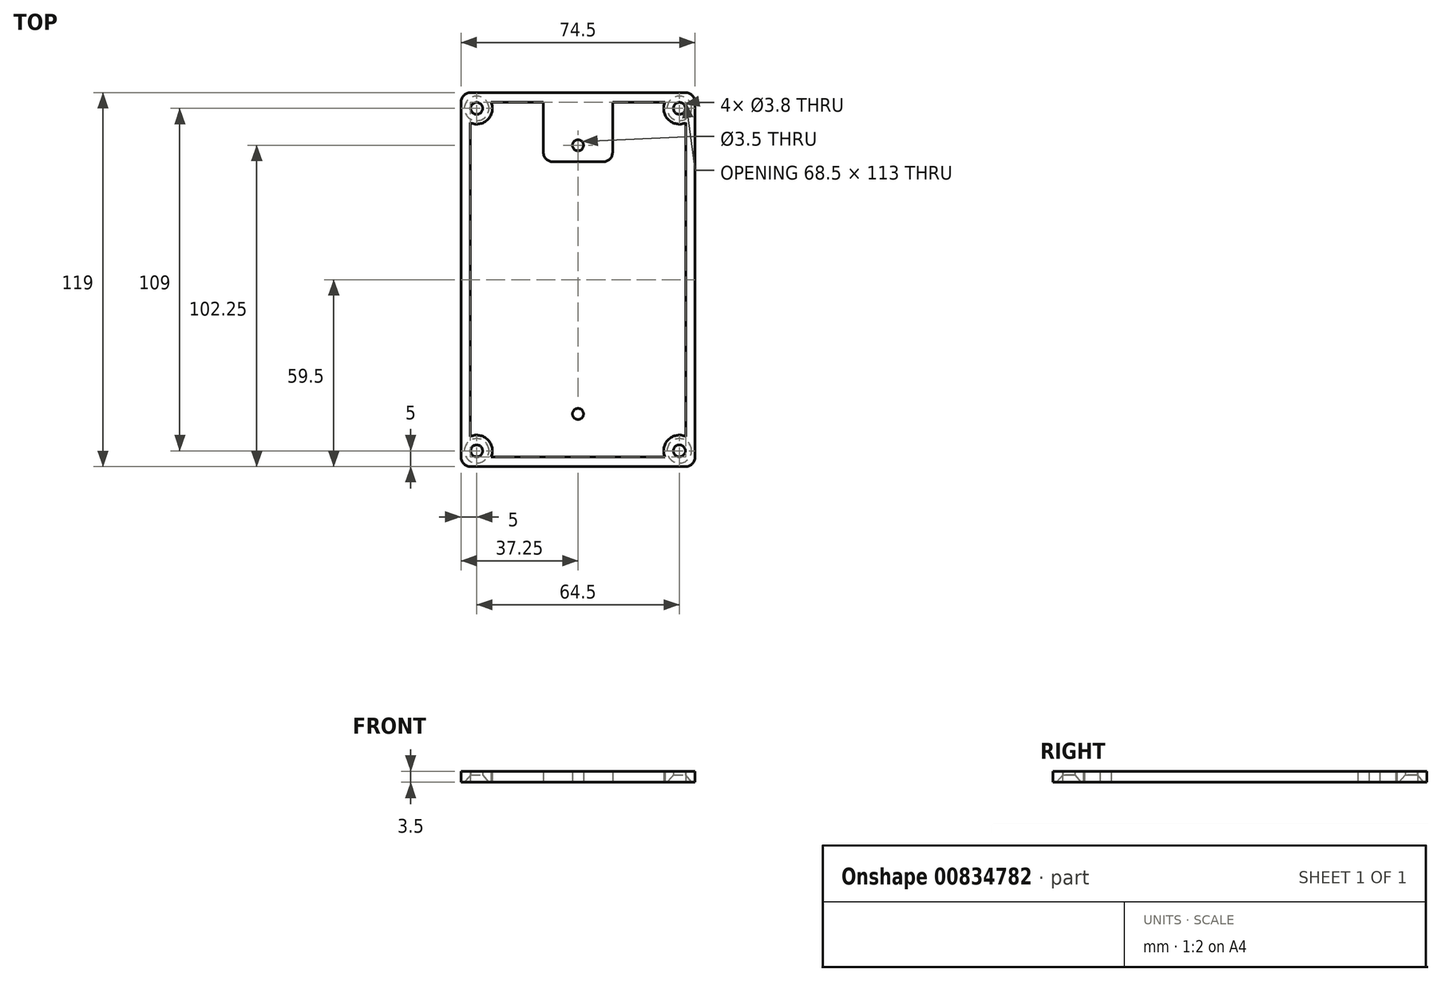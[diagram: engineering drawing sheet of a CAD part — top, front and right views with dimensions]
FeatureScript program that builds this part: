
annotation { "Feature Type Name" : "Feature", "Feature Type Description" : "" }
export const myFeature = defineFeature(function(context is Context, id is Id, definition is map)
    precondition{}
    {
        {
            var Q0;
            Q0=qCreatedBy(makeId("Top.planeOp"),FACE);
            var sketch = newSketch(context, id + "F0", { "sketchPlane" : qUnion([Q0])});
            skLineSegment(sketch, "E0.bottom", {"start": v(-37.25, 59.5) * mm, "end": v(37.25, 59.5) * mm});
            skLineSegment(sketch, "E0.top", {"start": v(-37.25, -59.5) * mm, "end": v(37.25, -59.5) * mm});
            skLineSegment(sketch, "E0.left", {"start": v(-37.25, 59.5) * mm, "end": v(-37.25, -59.5) * mm});
            skLineSegment(sketch, "E0.right", {"start": v(37.25, 59.5) * mm, "end": v(37.25, -59.5) * mm});
            skPoint(sketch, "E0.middle", {"position": v(0, 0) * mm});
            skLineSegment(sketch, "E1.bottom", {"start": v(-34.25, 56.5) * mm, "end": v(34.25, 56.5) * mm});
            skLineSegment(sketch, "E1.top", {"start": v(-34.25, -56.5) * mm, "end": v(34.25, -56.5) * mm});
            skLineSegment(sketch, "E1.left", {"start": v(-34.25, 56.5) * mm, "end": v(-34.25, -56.5) * mm});
            skLineSegment(sketch, "E1.right", {"start": v(34.25, 56.5) * mm, "end": v(34.25, -56.5) * mm});
            skCircle(sketch, "E2", {"center": v(-32.25, 54.5) * mm, "radius": 5 * mm});
            skPoint(sketch, "E2.first.point", {"position": v(-32.25, 59.5) * mm});
            skPoint(sketch, "E2.second.point", {"position": v(-33.16, 49.58) * mm});
            skPoint(sketch, "E2.third.point", {"position": v(-27.94, 51.97) * mm});
            skCircle(sketch, "E3", {"center": v(-32.25, 54.5) * mm, "radius": 1.9 * mm});
            skCircle(sketch, "E4.MirrorC", {"center": v(-32.25, -54.5) * mm, "radius": 5 * mm});
            skCircle(sketch, "E5.MirrorC", {"center": v(-32.25, -54.5) * mm, "radius": 1.9 * mm});
            skCircle(sketch, "E6.MirrorC", {"center": v(32.25, -54.5) * mm, "radius": 5 * mm});
            skCircle(sketch, "E7.MirrorC", {"center": v(32.25, -54.5) * mm, "radius": 1.9 * mm});
            skCircle(sketch, "E8.MirrorC", {"center": v(32.25, 54.5) * mm, "radius": 5 * mm});
            skCircle(sketch, "E9.MirrorC", {"center": v(32.25, 54.5) * mm, "radius": 1.9 * mm});
            skCircle(sketch, "E10", {"center": v(0, 42.75) * mm, "radius": 1.75 * mm});
            skPoint(sketch, "E10.centerSnap0", {"position": v(0, 59.5) * mm});
            skCircle(sketch, "E11.MirrorC", {"center": v(0, -42.75) * mm, "radius": 1.75 * mm});
            skLineSegment(sketch, "E12", {"start": v(-11, 56.5) * mm, "end": v(-11, 37.5) * mm});
            skLineSegment(sketch, "E13", {"start": v(-11, 37.5) * mm, "end": v(11, 37.5) * mm});
            skLineSegment(sketch, "E14", {"start": v(11, 37.5) * mm, "end": v(11, 56.5) * mm});
            skPoint(sketch, "E15", {"position": v(0, 37.5) * mm});
            skLineSegment(sketch, "E16.MirrorCS", {"start": v(11, -37.5) * mm, "end": v(11, -56.5) * mm});
            skLineSegment(sketch, "E17.MirrorCS", {"start": v(-11, -56.5) * mm, "end": v(-11, -37.5) * mm});
            skLineSegment(sketch, "E18.MirrorCS", {"start": v(-11, -37.5) * mm, "end": v(11, -37.5) * mm});
            skSolve(sketch);
        }
        {
            var Q0;
            {var subQ0=sQuery(id+"F0.wireOp",EDGE,"E0.left");var subQ1=sQuery(id+"F0.wireOp",EDGE,"E0.bottom");var subQ2=makeQuery(id+"F0.imprint","INTERSECT",VERTEX,{"derivedFrom":[subQ1,subQ0]});Q0=makeQuery(id+"F0.imprint","IMPRINT",FACE,{"disambiguationData":[TD([[makeQuery(id+"F0.imprint","IMPRINT",EDGE,{"disambiguationData":[TD([[subQ2,-1.0]])],"derivedFrom":subQ1}),-1.0]])]});}
            var Q1;
            {var subQ0=sQuery(id+"F0.wireOp",EDGE,"E0.right");var subQ1=sQuery(id+"F0.wireOp",EDGE,"E0.bottom");var subQ2=makeQuery(id+"F0.imprint","INTERSECT",VERTEX,{"derivedFrom":[subQ1,subQ0]});Q1=makeQuery(id+"F0.imprint","IMPRINT",FACE,{"disambiguationData":[TD([[makeQuery(id+"F0.imprint","IMPRINT",EDGE,{"disambiguationData":[TD([[subQ2,1.0]])],"derivedFrom":subQ1}),-1.0]])]});}
            var Q2;
            {var subQ0=sQuery(id+"F0.wireOp",EDGE,"E0.left");var subQ1=sQuery(id+"F0.wireOp",EDGE,"E0.top");var subQ2=makeQuery(id+"F0.imprint","INTERSECT",VERTEX,{"derivedFrom":[subQ1,subQ0]});Q2=makeQuery(id+"F0.imprint","IMPRINT",FACE,{"disambiguationData":[TD([[makeQuery(id+"F0.imprint","IMPRINT",EDGE,{"disambiguationData":[TD([[subQ2,-1.0]])],"derivedFrom":subQ1}),1.0]])]});}
            var Q3;
            {var subQ0=sQuery(id+"F0.wireOp",EDGE,"E0.right");var subQ1=sQuery(id+"F0.wireOp",EDGE,"E0.top");var subQ2=makeQuery(id+"F0.imprint","INTERSECT",VERTEX,{"derivedFrom":[subQ1,subQ0]});Q3=makeQuery(id+"F0.imprint","IMPRINT",FACE,{"disambiguationData":[TD([[makeQuery(id+"F0.imprint","IMPRINT",EDGE,{"disambiguationData":[TD([[subQ2,1.0]])],"derivedFrom":subQ1}),1.0]])]});}
            var Q4;
            {var subQ0=sQuery(id+"F0.wireOp",EDGE,"E2");var subQ1=sQuery(id+"F0.wireOp",EDGE,"E0.bottom");var subQ2=makeQuery(id+"F0.imprint","INTERSECT",VERTEX,{"derivedFrom":[subQ1,subQ0]});Q4=makeQuery(id+"F0.imprint","IMPRINT",FACE,{"disambiguationData":[TD([[makeQuery(id+"F0.imprint","IMPRINT",EDGE,{"disambiguationData":[TD([[subQ2,-1.0]])],"derivedFrom":subQ1}),-1.0]])]});}
            var Q5;
            {var subQ0=sQuery(id+"F0.wireOp",EDGE,"E4.MirrorC");var subQ1=sQuery(id+"F0.wireOp",EDGE,"E0.top");var subQ2=makeQuery(id+"F0.imprint","INTERSECT",VERTEX,{"derivedFrom":[subQ1,subQ0]});Q5=makeQuery(id+"F0.imprint","IMPRINT",FACE,{"disambiguationData":[TD([[makeQuery(id+"F0.imprint","IMPRINT",EDGE,{"disambiguationData":[TD([[subQ2,-1.0]])],"derivedFrom":subQ1}),1.0]])]});}
            var Q6;
            {var subQ0=sQuery(id+"F0.wireOp",EDGE,"E2");var subQ1=sQuery(id+"F0.wireOp",EDGE,"E0.left");var subQ2=makeQuery(id+"F0.imprint","INTERSECT",VERTEX,{"derivedFrom":[subQ1,subQ0]});Q6=makeQuery(id+"F0.imprint","IMPRINT",FACE,{"disambiguationData":[TD([[makeQuery(id+"F0.imprint","IMPRINT",EDGE,{"disambiguationData":[TD([[subQ2,-1.0]])],"derivedFrom":subQ1}),1.0]])]});}
            var Q7;
            {var subQ0=sQuery(id+"F0.wireOp",EDGE,"E8.MirrorC");var subQ1=sQuery(id+"F0.wireOp",EDGE,"E0.right");var subQ2=makeQuery(id+"F0.imprint","INTERSECT",VERTEX,{"derivedFrom":[subQ1,subQ0]});Q7=makeQuery(id+"F0.imprint","IMPRINT",FACE,{"disambiguationData":[TD([[makeQuery(id+"F0.imprint","IMPRINT",EDGE,{"disambiguationData":[TD([[subQ2,-1.0]])],"derivedFrom":subQ1}),-1.0]])]});}
            var Q8;
            {var subQ1=sQuery(id+"F0.wireOp",EDGE,"E1.left");var subQ5=sQuery(id+"F0.wireOp",EDGE,"E1.bottom");var subQ6=makeQuery(id+"F0.imprint","INTERSECT",VERTEX,{"derivedFrom":[subQ5,subQ1]});Q8=makeQuery(id+"F0.imprint","IMPRINT",FACE,{"disambiguationData":[TD([[makeQuery(id+"F0.imprint","IMPRINT",EDGE,{"disambiguationData":[TD([[subQ6,-1.0]])],"derivedFrom":subQ5}),1.0]])]});}
            var Q9;
            {var subQ1=sQuery(id+"F0.wireOp",EDGE,"E1.top");var subQ5=sQuery(id+"F0.wireOp",EDGE,"E6.MirrorC");var subQ10=makeQuery(id+"F0.imprint","INTERSECT",VERTEX,{"derivedFrom":[subQ1,subQ5]});Q9=makeQuery(id+"F0.imprint","IMPRINT",FACE,{"disambiguationData":[TD([[makeQuery(id+"F0.imprint","IMPRINT",EDGE,{"disambiguationData":[TD([[subQ10,-1.0]])],"derivedFrom":subQ1}),-1.0]])]});}
            var Q10;
            {var subQ0=sQuery(id+"F0.wireOp",EDGE,"E3");var subQ1=sQuery(id+"F0.wireOp",EDGE,"E1.bottom");var subQ2=makeQuery(id+"F0.imprint","INTERSECT",VERTEX,{"disambiguationData":[OD(0.0)],"derivedFrom":[subQ1,subQ0]});Q10=makeQuery(id+"F0.imprint","IMPRINT",FACE,{"disambiguationData":[TD([[makeQuery(id+"F0.imprint","IMPRINT",EDGE,{"disambiguationData":[TD([[subQ2,-1.0]])],"derivedFrom":subQ1}),1.0]])]});}
            var Q11;
            {var subQ0=sQuery(id+"F0.wireOp",EDGE,"E1.left");var subQ1=sQuery(id+"F0.wireOp",EDGE,"E1.bottom");var subQ2=makeQuery(id+"F0.imprint","INTERSECT",VERTEX,{"derivedFrom":[subQ1,subQ0]});Q11=makeQuery(id+"F0.imprint","IMPRINT",FACE,{"disambiguationData":[TD([[makeQuery(id+"F0.imprint","IMPRINT",EDGE,{"disambiguationData":[TD([[subQ2,-1.0]])],"derivedFrom":subQ1}),-1.0]])]});}
            var Q12;
            {var subQ0=sQuery(id+"F0.wireOp",EDGE,"E3");var subQ1=sQuery(id+"F0.wireOp",EDGE,"E1.left");var subQ2=makeQuery(id+"F0.imprint","INTERSECT",VERTEX,{"disambiguationData":[OD(0.0)],"derivedFrom":[subQ1,subQ0]});Q12=makeQuery(id+"F0.imprint","IMPRINT",FACE,{"disambiguationData":[TD([[makeQuery(id+"F0.imprint","IMPRINT",EDGE,{"disambiguationData":[TD([[subQ2,-1.0]])],"derivedFrom":subQ1}),-1.0]])]});}
            var Q13;
            {var subQ0=sQuery(id+"F0.wireOp",EDGE,"E1.left");var subQ1=sQuery(id+"F0.wireOp",EDGE,"E1.top");var subQ2=makeQuery(id+"F0.imprint","INTERSECT",VERTEX,{"derivedFrom":[subQ1,subQ0]});Q13=makeQuery(id+"F0.imprint","IMPRINT",FACE,{"disambiguationData":[TD([[makeQuery(id+"F0.imprint","IMPRINT",EDGE,{"disambiguationData":[TD([[subQ2,-1.0]])],"derivedFrom":subQ1}),1.0]])]});}
            var Q14;
            {var subQ0=sQuery(id+"F0.wireOp",EDGE,"E1.left");var subQ1=sQuery(id+"F0.wireOp",EDGE,"E1.top");var subQ2=makeQuery(id+"F0.imprint","INTERSECT",VERTEX,{"derivedFrom":[subQ1,subQ0]});Q14=makeQuery(id+"F0.imprint","IMPRINT",FACE,{"disambiguationData":[TD([[makeQuery(id+"F0.imprint","IMPRINT",EDGE,{"disambiguationData":[TD([[subQ2,-1.0]])],"derivedFrom":subQ1}),-1.0]])]});}
            var Q15;
            {var subQ0=sQuery(id+"F0.wireOp",EDGE,"E5.MirrorC");var subQ1=sQuery(id+"F0.wireOp",EDGE,"E1.top");var subQ2=makeQuery(id+"F0.imprint","INTERSECT",VERTEX,{"disambiguationData":[OD(0.0)],"derivedFrom":[subQ1,subQ0]});Q15=makeQuery(id+"F0.imprint","IMPRINT",FACE,{"disambiguationData":[TD([[makeQuery(id+"F0.imprint","IMPRINT",EDGE,{"disambiguationData":[TD([[subQ2,-1.0]])],"derivedFrom":subQ1}),-1.0]])]});}
            var Q16;
            {var subQ0=sQuery(id+"F0.wireOp",EDGE,"E5.MirrorC");var subQ1=sQuery(id+"F0.wireOp",EDGE,"E1.left");var subQ2=makeQuery(id+"F0.imprint","INTERSECT",VERTEX,{"disambiguationData":[OD(0.0)],"derivedFrom":[subQ1,subQ0]});Q16=makeQuery(id+"F0.imprint","IMPRINT",FACE,{"disambiguationData":[TD([[makeQuery(id+"F0.imprint","IMPRINT",EDGE,{"disambiguationData":[TD([[subQ2,-1.0]])],"derivedFrom":subQ1}),-1.0]])]});}
            var Q17;
            {var subQ0=sQuery(id+"F0.wireOp",EDGE,"E6.MirrorC");var subQ1=sQuery(id+"F0.wireOp",EDGE,"E1.top");var subQ2=makeQuery(id+"F0.imprint","INTERSECT",VERTEX,{"derivedFrom":[subQ1,subQ0]});Q17=makeQuery(id+"F0.imprint","IMPRINT",FACE,{"disambiguationData":[TD([[makeQuery(id+"F0.imprint","IMPRINT",EDGE,{"disambiguationData":[TD([[subQ2,-1.0]])],"derivedFrom":subQ1}),1.0]])]});}
            var Q18;
            {var subQ0=sQuery(id+"F0.wireOp",EDGE,"E1.right");var subQ1=sQuery(id+"F0.wireOp",EDGE,"E1.top");var subQ2=makeQuery(id+"F0.imprint","INTERSECT",VERTEX,{"derivedFrom":[subQ1,subQ0]});Q18=makeQuery(id+"F0.imprint","IMPRINT",FACE,{"disambiguationData":[TD([[makeQuery(id+"F0.imprint","IMPRINT",EDGE,{"disambiguationData":[TD([[subQ2,1.0]])],"derivedFrom":subQ1}),1.0]])]});}
            var Q19;
            {var subQ0=sQuery(id+"F0.wireOp",EDGE,"E7.MirrorC");var subQ1=sQuery(id+"F0.wireOp",EDGE,"E1.right");var subQ2=makeQuery(id+"F0.imprint","INTERSECT",VERTEX,{"disambiguationData":[OD(0.0)],"derivedFrom":[subQ1,subQ0]});Q19=makeQuery(id+"F0.imprint","IMPRINT",FACE,{"disambiguationData":[TD([[makeQuery(id+"F0.imprint","IMPRINT",EDGE,{"disambiguationData":[TD([[subQ2,-1.0]])],"derivedFrom":subQ1}),1.0]])]});}
            var Q20;
            {var subQ0=sQuery(id+"F0.wireOp",EDGE,"E7.MirrorC");var subQ1=sQuery(id+"F0.wireOp",EDGE,"E1.top");var subQ2=makeQuery(id+"F0.imprint","INTERSECT",VERTEX,{"disambiguationData":[OD(0.0)],"derivedFrom":[subQ1,subQ0]});Q20=makeQuery(id+"F0.imprint","IMPRINT",FACE,{"disambiguationData":[TD([[makeQuery(id+"F0.imprint","IMPRINT",EDGE,{"disambiguationData":[TD([[subQ2,-1.0]])],"derivedFrom":subQ1}),-1.0]])]});}
            var Q21;
            {var subQ0=sQuery(id+"F0.wireOp",EDGE,"E1.right");var subQ1=sQuery(id+"F0.wireOp",EDGE,"E1.bottom");var subQ2=makeQuery(id+"F0.imprint","INTERSECT",VERTEX,{"derivedFrom":[subQ1,subQ0]});Q21=makeQuery(id+"F0.imprint","IMPRINT",FACE,{"disambiguationData":[TD([[makeQuery(id+"F0.imprint","IMPRINT",EDGE,{"disambiguationData":[TD([[subQ2,1.0]])],"derivedFrom":subQ1}),-1.0]])]});}
            var Q22;
            {var subQ0=sQuery(id+"F0.wireOp",EDGE,"E9.MirrorC");var subQ1=sQuery(id+"F0.wireOp",EDGE,"E1.bottom");var subQ2=makeQuery(id+"F0.imprint","INTERSECT",VERTEX,{"disambiguationData":[OD(0.0)],"derivedFrom":[subQ1,subQ0]});Q22=makeQuery(id+"F0.imprint","IMPRINT",FACE,{"disambiguationData":[TD([[makeQuery(id+"F0.imprint","IMPRINT",EDGE,{"disambiguationData":[TD([[subQ2,-1.0]])],"derivedFrom":subQ1}),1.0]])]});}
            var Q23;
            {var subQ3=sQuery(id+"F0.wireOp",EDGE,"E8.MirrorC");var subQ5=sQuery(id+"F0.wireOp",EDGE,"E1.bottom");var subQ11=makeQuery(id+"F0.imprint","INTERSECT",VERTEX,{"derivedFrom":[subQ5,subQ3]});Q23=makeQuery(id+"F0.imprint","IMPRINT",FACE,{"disambiguationData":[TD([[makeQuery(id+"F0.imprint","IMPRINT",EDGE,{"disambiguationData":[TD([[subQ11,-1.0]])],"derivedFrom":subQ5}),1.0]])]});}
            var Q24;
            {var subQ0=sQuery(id+"F0.wireOp",EDGE,"E9.MirrorC");var subQ1=sQuery(id+"F0.wireOp",EDGE,"E1.right");var subQ2=makeQuery(id+"F0.imprint","INTERSECT",VERTEX,{"disambiguationData":[OD(0.0)],"derivedFrom":[subQ1,subQ0]});Q24=makeQuery(id+"F0.imprint","IMPRINT",FACE,{"disambiguationData":[TD([[makeQuery(id+"F0.imprint","IMPRINT",EDGE,{"disambiguationData":[TD([[subQ2,-1.0]])],"derivedFrom":subQ1}),1.0]])]});}
            var Q25;
            {var subQ0=sQuery(id+"F0.wireOp",EDGE,"E8.MirrorC");var subQ1=sQuery(id+"F0.wireOp",EDGE,"E1.bottom");var subQ2=makeQuery(id+"F0.imprint","INTERSECT",VERTEX,{"derivedFrom":[subQ1,subQ0]});Q25=makeQuery(id+"F0.imprint","IMPRINT",FACE,{"disambiguationData":[TD([[makeQuery(id+"F0.imprint","IMPRINT",EDGE,{"disambiguationData":[TD([[subQ2,-1.0]])],"derivedFrom":subQ1}),-1.0]])]});}
            var Q26;
            Q26=makeQuery(id+"F0.imprint","IMPRINT",FACE,{"disambiguationData":[TD([[makeQuery(id+"F0.imprint","IMPRINT",EDGE,{"derivedFrom":sQuery(id+"F0.wireOp",EDGE,"E3")}),1.0]])]});
            var Q27;
            Q27=makeQuery(id+"F0.imprint","IMPRINT",FACE,{"disambiguationData":[TD([[makeQuery(id+"F0.imprint","IMPRINT",EDGE,{"derivedFrom":sQuery(id+"F0.wireOp",EDGE,"E9.MirrorC")}),-1.0]])]});
            var Q28;
            Q28=makeQuery(id+"F0.imprint","IMPRINT",FACE,{"disambiguationData":[TD([[makeQuery(id+"F0.imprint","IMPRINT",EDGE,{"derivedFrom":sQuery(id+"F0.wireOp",EDGE,"E5.MirrorC")}),-1.0]])]});
            var Q29;
            Q29=makeQuery(id+"F0.imprint","IMPRINT",FACE,{"disambiguationData":[TD([[makeQuery(id+"F0.imprint","IMPRINT",EDGE,{"derivedFrom":sQuery(id+"F0.wireOp",EDGE,"E7.MirrorC")}),1.0]])]});
            extrude(context, id + "F1", {"entities" : qUnion([Q0, Q1, Q2, Q3, Q4, Q5, Q6, Q7, Q8, Q9, Q10, Q11, Q12, Q13, Q14, Q15, Q16, Q17, Q18, Q19, Q20, Q21, Q22, Q23, Q24, Q25, Q26, Q27, Q28, Q29]), "depth" : 3.5 * mm, "offsetDistance" : 25 * mm});
        }
        {
            var Q0;
            Q0=makeQuery(id+"F1.opExtrude","SWEPT_EDGE",EDGE,{"disambiguationData":[OSD([sQuery(id+"F0.wireOp",EDGE,"E0.bottom"),sQuery(id+"F0.wireOp",EDGE,"E0.left")])]});
            var Q1;
            Q1=makeQuery(id+"F1.opExtrude","SWEPT_EDGE",EDGE,{"disambiguationData":[OSD([sQuery(id+"F0.wireOp",EDGE,"E0.bottom"),sQuery(id+"F0.wireOp",EDGE,"E0.right")])]});
            var Q2;
            Q2=makeQuery(id+"F1.opExtrude","SWEPT_EDGE",EDGE,{"disambiguationData":[OSD([sQuery(id+"F0.wireOp",EDGE,"E0.top"),sQuery(id+"F0.wireOp",EDGE,"E0.right")])]});
            var Q3;
            Q3=makeQuery(id+"F1.opExtrude","SWEPT_EDGE",EDGE,{"disambiguationData":[OSD([sQuery(id+"F0.wireOp",EDGE,"E0.top"),sQuery(id+"F0.wireOp",EDGE,"E0.left")])]});
            fillet(context, id + "F2", {"entities" : qUnion([Q0, Q1, Q2, Q3]), "radius" : 3 * mm, "tangentPropagation" : true, "allowEdgeOverflow" : false});
        }
        {
            var Q0;
            Q0=makeQuery(id+"F0.imprint","IMPRINT",FACE,{"disambiguationData":[TD([[makeQuery(id+"F0.imprint","IMPRINT",EDGE,{"derivedFrom":sQuery(id+"F0.wireOp",EDGE,"E10")}),-1.0]])]});
            var Q1;
            Q1=makeQuery(id+"F0.imprint","IMPRINT",FACE,{"disambiguationData":[TD([[makeQuery(id+"F0.imprint","IMPRINT",EDGE,{"derivedFrom":sQuery(id+"F0.wireOp",EDGE,"E11.MirrorC")}),1.0]])]});
            extrude(context, id + "F3", {"entities" : qUnion([Q0, Q1]), "operationType" : NewBodyOperationType.ADD, "depth" : 3.5 * mm, "offsetDistance" : 25 * mm});
        }
        {
            var Q0;
            Q0=sQuery(id+"F0.wireOp",VERTEX,"E2.center");
            var Q1;
            Q1=sQuery(id+"F0.wireOp",VERTEX,"E9.MirrorC.center");
            var Q2;
            Q2=sQuery(id+"F0.wireOp",VERTEX,"E6.MirrorC.center");
            var Q3;
            Q3=sQuery(id+"F0.wireOp",VERTEX,"E5.MirrorC.center");
            var Q4;
            Q4=makeQuery(id+"F1.opExtrude","SWEPT_BODY",BODY,{"disambiguationData":[OSD([sQuery(id+"F0.wireOp",EDGE,"E0.bottom"),sQuery(id+"F0.wireOp",EDGE,"E0.top"),sQuery(id+"F0.wireOp",EDGE,"E0.left"),sQuery(id+"F0.wireOp",EDGE,"E0.right"),sQuery(id+"F0.wireOp",EDGE,"E1.bottom"),sQuery(id+"F0.wireOp",EDGE,"E1.top"),sQuery(id+"F0.wireOp",EDGE,"E1.left"),sQuery(id+"F0.wireOp",EDGE,"E1.right"),sQuery(id+"F0.wireOp",EDGE,"E2"),sQuery(id+"F0.wireOp",EDGE,"E4.MirrorC"),sQuery(id+"F0.wireOp",EDGE,"E6.MirrorC"),sQuery(id+"F0.wireOp",EDGE,"E8.MirrorC")])]});
            hole(context, id + "F4", {"style" : HoleStyle.C_SINK, "endStyle" : HoleEndStyle.BLIND, "oppositeDirection" : true, "standardTappedOrClearance" : lookupTablePath({ "standard" : "ANSI", "fit" : "Normal (ASME)", "size" : "#6", "type" : "Clearance" }), "standardBlindInLast" : lookupTablePath({ "fit" : "Free", "standard" : "ANSI", "size" : "#6", "type" : "Clearance" }), "holeDiameter" : 3.8 * mm, "cSinkDiameter" : 7.8 * mm, "cSinkAngle" : 82 * degree, "majorDiameter" : 3.5 * mm, "holeDepth" : 14.38 * mm, "tappedDepth" : 12 * mm, "tapClearance" : 3, "locations" : qUnion([Q0, Q1, Q2, Q3]), "scope" : qUnion([Q4])});
        }
        {
            var Q0;
            Q0=makeQuery(id+"F3.opExtrude","SWEPT_EDGE",EDGE,{"disambiguationData":[OSD([sQuery(id+"F0.wireOp",EDGE,"E12"),sQuery(id+"F0.wireOp",EDGE,"E13")])]});
            var Q1;
            Q1=makeQuery(id+"F3.opExtrude","SWEPT_EDGE",EDGE,{"disambiguationData":[OSD([sQuery(id+"F0.wireOp",EDGE,"E13"),sQuery(id+"F0.wireOp",EDGE,"E14")])]});
            var Q2;
            Q2=makeQuery(id+"F3.opExtrude","SWEPT_EDGE",EDGE,{"disambiguationData":[OSD([sQuery(id+"F0.wireOp",EDGE,"E16.MirrorCS"),sQuery(id+"F0.wireOp",EDGE,"E18.MirrorCS")])]});
            var Q3;
            Q3=makeQuery(id+"F3.opExtrude","SWEPT_EDGE",EDGE,{"disambiguationData":[OSD([sQuery(id+"F0.wireOp",EDGE,"E17.MirrorCS"),sQuery(id+"F0.wireOp",EDGE,"E18.MirrorCS")])]});
            fillet(context, id + "F5", {"entities" : qUnion([Q0, Q1, Q2, Q3]), "radius" : 3 * mm, "tangentPropagation" : true, "allowEdgeOverflow" : false});
        }
    });
